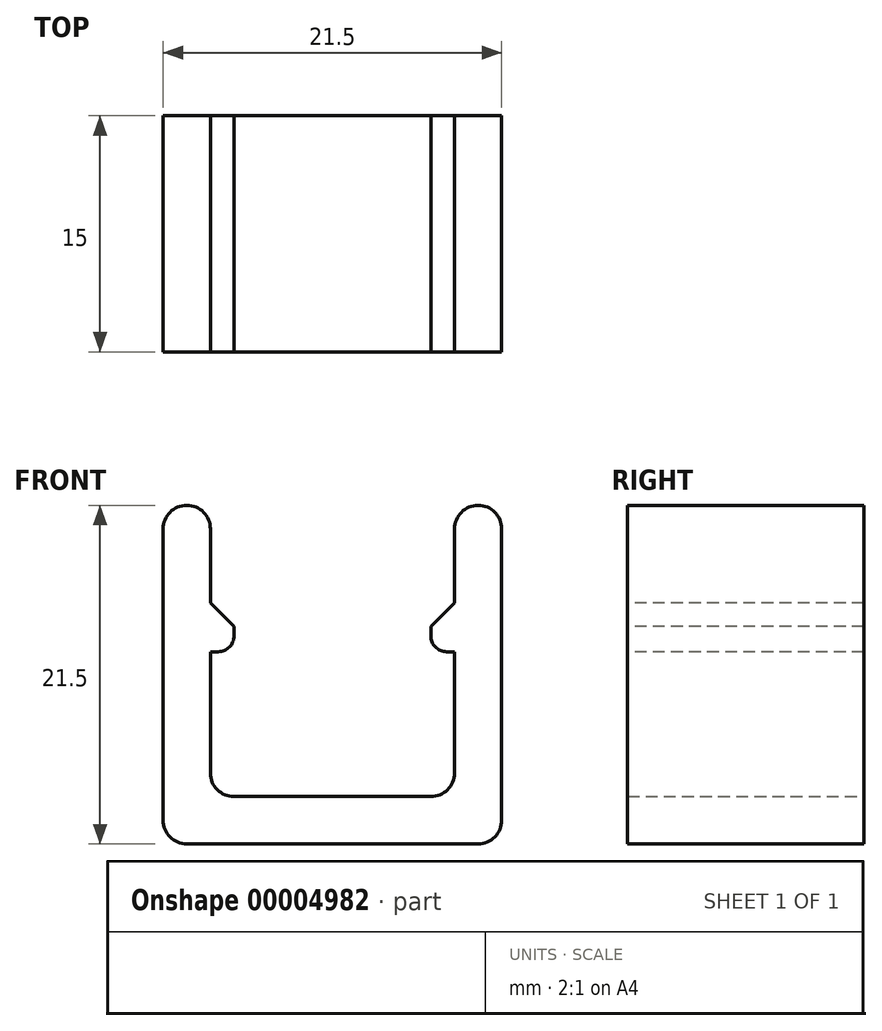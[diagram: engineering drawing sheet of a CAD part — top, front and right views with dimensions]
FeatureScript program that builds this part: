
annotation { "Feature Type Name" : "Feature", "Feature Type Description" : "" }
export const myFeature = defineFeature(function(context is Context, id is Id, definition is map)
    precondition{}
    {
        {
            var Q0;
            Q0=qCreatedBy(makeId("Front.planeOp"),FACE);
            var sketch = newSketch(context, id + "F0", { "sketchPlane" : qUnion([Q0])});
            skLineSegment(sketch, "E0", {"start": v(0, 0) * mm, "end": v(0, 15.32) * mm, "construction": true});
            skLineSegment(sketch, "E1.rect.bottom", {"start": v(7.75, 7.75) * mm, "end": v(-7.75, 7.75) * mm, "construction": true});
            skLineSegment(sketch, "E1.rect.top", {"start": v(7.75, -7.75) * mm, "end": v(-7.75, -7.75) * mm, "construction": true});
            skLineSegment(sketch, "E1.rect.left", {"start": v(7.75, 7.75) * mm, "end": v(7.75, -7.75) * mm});
            skLineSegment(sketch, "E1.rect.right", {"start": v(-7.75, 7.75) * mm, "end": v(-7.75, -7.75) * mm});
            skPoint(sketch, "E1.rect.middle", {"position": v(0, 0) * mm});
            skLineSegment(sketch, "E2", {"start": v(-7.75, 7.75) * mm, "end": v(-10.75, 7.75) * mm});
            skLineSegment(sketch, "E3", {"start": v(-10.75, 7.75) * mm, "end": v(-10.75, -13.75) * mm});
            skLineSegment(sketch, "E4", {"start": v(7.75, 7.75) * mm, "end": v(10.75, 7.75) * mm});
            skLineSegment(sketch, "E5", {"start": v(10.75, 7.75) * mm, "end": v(10.75, -13.75) * mm});
            skLineSegment(sketch, "E6", {"start": v(10.75, -13.75) * mm, "end": v(-10.75, -13.75) * mm});
            skLineSegment(sketch, "E7", {"start": v(-7.75, -7.75) * mm, "end": v(-7.75, -10.75) * mm});
            skLineSegment(sketch, "E8", {"start": v(-7.75, -10.75) * mm, "end": v(7.75, -10.75) * mm});
            skLineSegment(sketch, "E9", {"start": v(7.75, -10.75) * mm, "end": v(7.75, -7.75) * mm});
            skSolve(sketch);
        }
        {
            var Q0;
            Q0=qSketchRegion(id+"F0",true);
            extrude(context, id + "F1", {"entities" : qUnion([Q0]), "depth" : 15 * mm});
        }
        {
            var Q0;
            Q0=makeQuery(id+"F1.opExtrude","CAP_FACE",FACE,{"disambiguationData":[OSD([sQuery(id+"F0.wireOp",EDGE,"E1.rect.left"),sQuery(id+"F0.wireOp",EDGE,"E1.rect.right"),sQuery(id+"F0.wireOp",EDGE,"E2"),sQuery(id+"F0.wireOp",EDGE,"E3"),sQuery(id+"F0.wireOp",EDGE,"E4"),sQuery(id+"F0.wireOp",EDGE,"E5"),sQuery(id+"F0.wireOp",EDGE,"E6"),sQuery(id+"F0.wireOp",EDGE,"E7"),sQuery(id+"F0.wireOp",EDGE,"E8"),sQuery(id+"F0.wireOp",EDGE,"E9")])],"isStart":false});
            var sketch = newSketch(context, id + "F2", { "sketchPlane" : qUnion([Q0])});
            skLineSegment(sketch, "E10", {"start": v(0, 0) * mm, "end": v(-7.75, 0) * mm, "construction": true});
            skLineSegment(sketch, "E11.bottom", {"start": v(-7.75, 1.55) * mm, "end": v(-6.25, 1.55) * mm});
            skLineSegment(sketch, "E11.top", {"start": v(-7.75, -1.55) * mm, "end": v(-6.25, -1.55) * mm});
            skLineSegment(sketch, "E11.left", {"start": v(-7.75, 1.55) * mm, "end": v(-7.75, -1.55) * mm});
            skLineSegment(sketch, "E11.right", {"start": v(-6.25, 1.55) * mm, "end": v(-6.25, -1.55) * mm});
            skPoint(sketch, "E12", {"position": v(-6.25, 0) * mm});
            skLineSegment(sketch, "E13", {"start": v(0, 0) * mm, "end": v(0, 15.8) * mm, "construction": true});
            skLineSegment(sketch, "E14.0.MirrorCS", {"start": v(7.75, -1.55) * mm, "end": v(6.25, -1.55) * mm});
            skLineSegment(sketch, "E14.1.MirrorCS", {"start": v(6.25, 1.55) * mm, "end": v(6.25, -1.55) * mm});
            skLineSegment(sketch, "E14.2.MirrorCS", {"start": v(7.75, 1.55) * mm, "end": v(7.75, -1.55) * mm});
            skLineSegment(sketch, "E14.3.MirrorCS", {"start": v(7.75, 1.55) * mm, "end": v(6.25, 1.55) * mm});
            skSolve(sketch);
        }
        {
            var Q0;
            Q0=qSketchRegion(id+"F2",true);
            var Q1;
            Q1=makeQuery(id+"F1.opExtrude","CAP_FACE",FACE,{"disambiguationData":[OSD([sQuery(id+"F0.wireOp",EDGE,"E1.rect.left"),sQuery(id+"F0.wireOp",EDGE,"E1.rect.right"),sQuery(id+"F0.wireOp",EDGE,"E2"),sQuery(id+"F0.wireOp",EDGE,"E3"),sQuery(id+"F0.wireOp",EDGE,"E4"),sQuery(id+"F0.wireOp",EDGE,"E5"),sQuery(id+"F0.wireOp",EDGE,"E6"),sQuery(id+"F0.wireOp",EDGE,"E7"),sQuery(id+"F0.wireOp",EDGE,"E8"),sQuery(id+"F0.wireOp",EDGE,"E9")])],"isStart":true});
            extrude(context, id + "F3", {"entities" : qUnion([Q0]), "operationType" : NewBodyOperationType.ADD, "endBound" : BoundingType.UP_TO_SURFACE, "oppositeDirection" : true, "endBoundEntityFace" : qUnion([Q1]), "depth" : 25 * mm});
        }
        {
            var Q0;
            Q0=makeQuery(id+"F1.opExtrude","SWEPT_EDGE",EDGE,{"disambiguationData":[OSD([sQuery(id+"F0.wireOp",EDGE,"E3"),sQuery(id+"F0.wireOp",EDGE,"E6")])]});
            var Q1;
            Q1=makeQuery(id+"F1.opExtrude","SWEPT_EDGE",EDGE,{"disambiguationData":[OSD([sQuery(id+"F0.wireOp",EDGE,"E5"),sQuery(id+"F0.wireOp",EDGE,"E6")])]});
            var Q2;
            Q2=makeQuery(id+"F1.opExtrude","SWEPT_EDGE",EDGE,{"disambiguationData":[OSD([sQuery(id+"F0.wireOp",EDGE,"E4"),sQuery(id+"F0.wireOp",EDGE,"E5")])]});
            var Q3;
            Q3=makeQuery(id+"F1.opExtrude","SWEPT_EDGE",EDGE,{"disambiguationData":[OSD([sQuery(id+"F0.wireOp",EDGE,"E2"),sQuery(id+"F0.wireOp",EDGE,"E3")])]});
            var Q4;
            Q4=makeQuery(id+"F1.opExtrude","SWEPT_EDGE",EDGE,{"disambiguationData":[OSD([sQuery(id+"F0.wireOp",EDGE,"E1.rect.left"),sQuery(id+"F0.wireOp",EDGE,"E4")])]});
            var Q5;
            Q5=makeQuery(id+"F1.opExtrude","SWEPT_EDGE",EDGE,{"disambiguationData":[OSD([sQuery(id+"F0.wireOp",EDGE,"E1.rect.right"),sQuery(id+"F0.wireOp",EDGE,"E2")])]});
            var Q6;
            Q6=makeQuery(id+"F1.opExtrude","SWEPT_EDGE",EDGE,{"disambiguationData":[OSD([sQuery(id+"F0.wireOp",EDGE,"E7"),sQuery(id+"F0.wireOp",EDGE,"E8")])]});
            var Q7;
            Q7=makeQuery(id+"F1.opExtrude","SWEPT_EDGE",EDGE,{"disambiguationData":[OSD([sQuery(id+"F0.wireOp",EDGE,"E8"),sQuery(id+"F0.wireOp",EDGE,"E9")])]});
            fillet(context, id + "F4", {"entities" : qUnion([Q0, Q1, Q2, Q3, Q4, Q5, Q6, Q7]), "radius" : 1.5 * mm, "tangentPropagation" : true, "allowEdgeOverflow" : false});
        }
        {
            var Q0;
            Q0=makeQuery(id+"F3.opExtrude","SWEPT_EDGE",EDGE,{"disambiguationData":[OSD([sQuery(id+"F2.wireOp",EDGE,"E11.top"),sQuery(id+"F2.wireOp",EDGE,"E11.right")])]});
            var Q1;
            Q1=makeQuery(id+"F3.opExtrude","SWEPT_EDGE",EDGE,{"disambiguationData":[OSD([sQuery(id+"F2.wireOp",EDGE,"E14.0.MirrorCS"),sQuery(id+"F2.wireOp",EDGE,"E14.1.MirrorCS")])]});
            fillet(context, id + "F5", {"entities" : qUnion([Q0, Q1]), "radius" : 1 * mm, "tangentPropagation" : true, "allowEdgeOverflow" : false});
        }
        {
            var Q0;
            Q0=makeQuery(id+"F3.opExtrude","SWEPT_EDGE",EDGE,{"disambiguationData":[OSD([sQuery(id+"F2.wireOp",EDGE,"E11.bottom"),sQuery(id+"F2.wireOp",EDGE,"E11.right")])]});
            var Q1;
            Q1=makeQuery(id+"F3.opExtrude","SWEPT_EDGE",EDGE,{"disambiguationData":[OSD([sQuery(id+"F2.wireOp",EDGE,"E14.1.MirrorCS"),sQuery(id+"F2.wireOp",EDGE,"E14.3.MirrorCS")])]});
            chamfer(context, id + "F6", {"entities" : qUnion([Q0, Q1]), "width" : 1.5 * mm, "tangentPropagation" : true});
        }
    });
